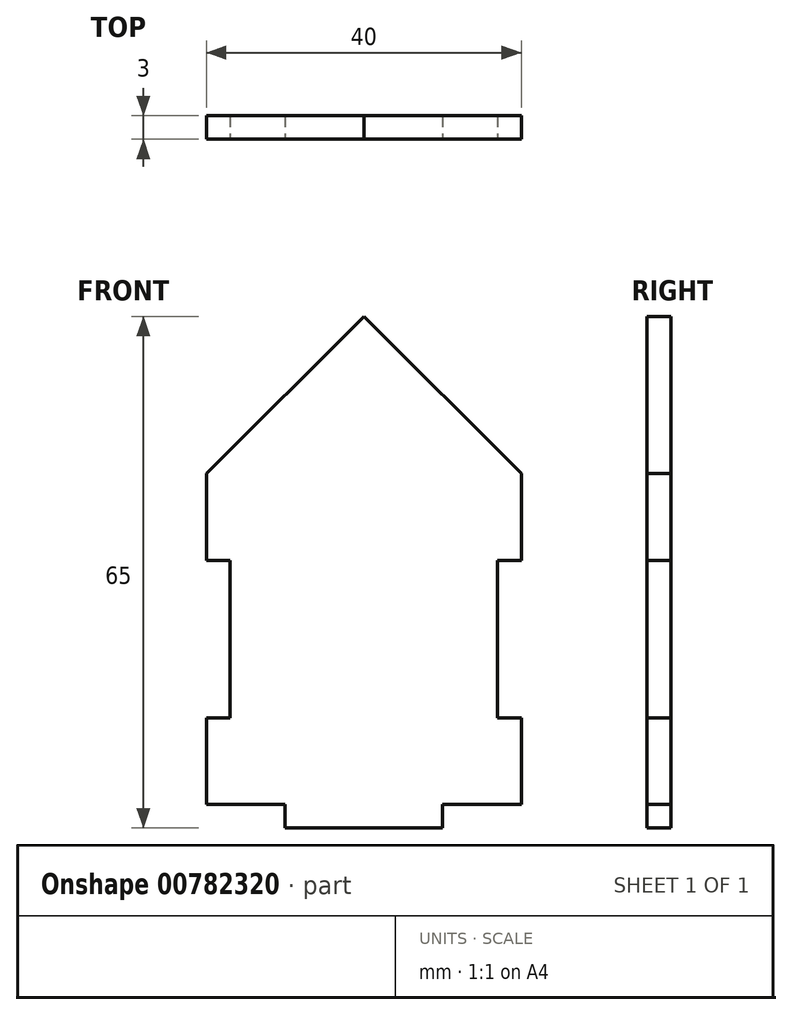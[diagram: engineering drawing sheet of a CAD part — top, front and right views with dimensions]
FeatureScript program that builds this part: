
annotation { "Feature Type Name" : "Feature", "Feature Type Description" : "" }
export const myFeature = defineFeature(function(context is Context, id is Id, definition is map)
    precondition{}
    {
        {
            var Q0;
            Q0=qCreatedBy(makeId("Front.planeOp"),FACE);
            var sketch = newSketch(context, id + "F0", { "sketchPlane" : qUnion([Q0])});
            skLineSegment(sketch, "E0.top", {"start": v(20, -21) * mm, "end": v(-20, -21) * mm});
            skPoint(sketch, "E0.middle", {"position": v(0, 0) * mm});
            skLineSegment(sketch, "E1", {"start": v(-10, -21) * mm, "end": v(-10, 19) * mm});
            skLineSegment(sketch, "E2", {"start": v(-10, 19) * mm, "end": v(10, 19) * mm});
            skLineSegment(sketch, "E3", {"start": v(10, 19) * mm, "end": v(10, -21) * mm});
            skLineSegment(sketch, "E4", {"start": v(-20, 21) * mm, "end": v(0, 41) * mm});
            skLineSegment(sketch, "E5", {"start": v(0, 41) * mm, "end": v(20, 21) * mm});
            skLineSegment(sketch, "E6", {"start": v(-20, 10) * mm, "end": v(-17, 10) * mm});
            skLineSegment(sketch, "E7", {"start": v(-17, 10) * mm, "end": v(-17, -10) * mm});
            skLineSegment(sketch, "E8", {"start": v(-17, -10) * mm, "end": v(-20, -10) * mm});
            skLineSegment(sketch, "E9", {"start": v(-20, 21) * mm, "end": v(-20, 10) * mm});
            skLineSegment(sketch, "E10", {"start": v(-20, -10) * mm, "end": v(-20, -21) * mm});
            skLineSegment(sketch, "E11", {"start": v(20, 21) * mm, "end": v(20, 10) * mm});
            skLineSegment(sketch, "E12", {"start": v(20, 10) * mm, "end": v(17, 10) * mm});
            skLineSegment(sketch, "E13", {"start": v(17, 10) * mm, "end": v(17, -10) * mm});
            skLineSegment(sketch, "E14", {"start": v(17, -10) * mm, "end": v(20, -10) * mm});
            skLineSegment(sketch, "E15", {"start": v(20, -10) * mm, "end": v(20, -21) * mm});
            skLineSegment(sketch, "E16", {"start": v(-10, -21) * mm, "end": v(-10, -24) * mm});
            skLineSegment(sketch, "E17", {"start": v(-10, -24) * mm, "end": v(10, -24) * mm});
            skLineSegment(sketch, "E18", {"start": v(10, -24) * mm, "end": v(10, -21) * mm});
            skSolve(sketch);
        }
        {
            var Q0;
            {var subQ12=sQuery(id+"F0.wireOp",EDGE,"E1");Q0=makeQuery(id+"F0.imprint","IMPRINT",FACE,{"disambiguationData":[TD([[makeQuery(id+"F0.imprint","IMPRINT",EDGE,{"derivedFrom":subQ12}),1.0]])]});}
            var Q1;
            {var subQ0=sQuery(id+"F0.wireOp",EDGE,"E1");Q1=makeQuery(id+"F0.imprint","IMPRINT",FACE,{"disambiguationData":[TD([[makeQuery(id+"F0.imprint","IMPRINT",EDGE,{"derivedFrom":subQ0}),-1.0]])]});}
            var Q2;
            {var subQ0=sQuery(id+"F0.wireOp",EDGE,"c90049ba-afea-4f03-8b41-77b7b003ae6d0.MirrorCS");Q2=makeQuery(id+"F0.imprint","IMPRINT",FACE,{"disambiguationData":[TD([[makeQuery(id+"F0.imprint","IMPRINT",EDGE,{"derivedFrom":subQ0}),1.0]])]});}
            var Q3;
            {var subQ0=sQuery(id+"F0.wireOp",EDGE,"Lv1DZn4h-48uY-n0iO-hpn6-IClfQAFSjkQm");Q3=makeQuery(id+"F0.imprint","IMPRINT",FACE,{"disambiguationData":[TD([[makeQuery(id+"F0.imprint","IMPRINT",EDGE,{"derivedFrom":subQ0}),-1.0]])]});}
            var Q4;
            {var subQ0=sQuery(id+"F0.wireOp",EDGE,"E16");Q4=makeQuery(id+"F0.imprint","IMPRINT",FACE,{"disambiguationData":[TD([[makeQuery(id+"F0.imprint","IMPRINT",EDGE,{"derivedFrom":subQ0}),1.0]])]});}
            extrude(context, id + "F1", {"entities" : qUnion([Q0, Q1, Q2, Q3, Q4]), "oppositeDirection" : true, "depth" : 3 * mm, "offsetDistance" : 25 * mm});
        }
    });
